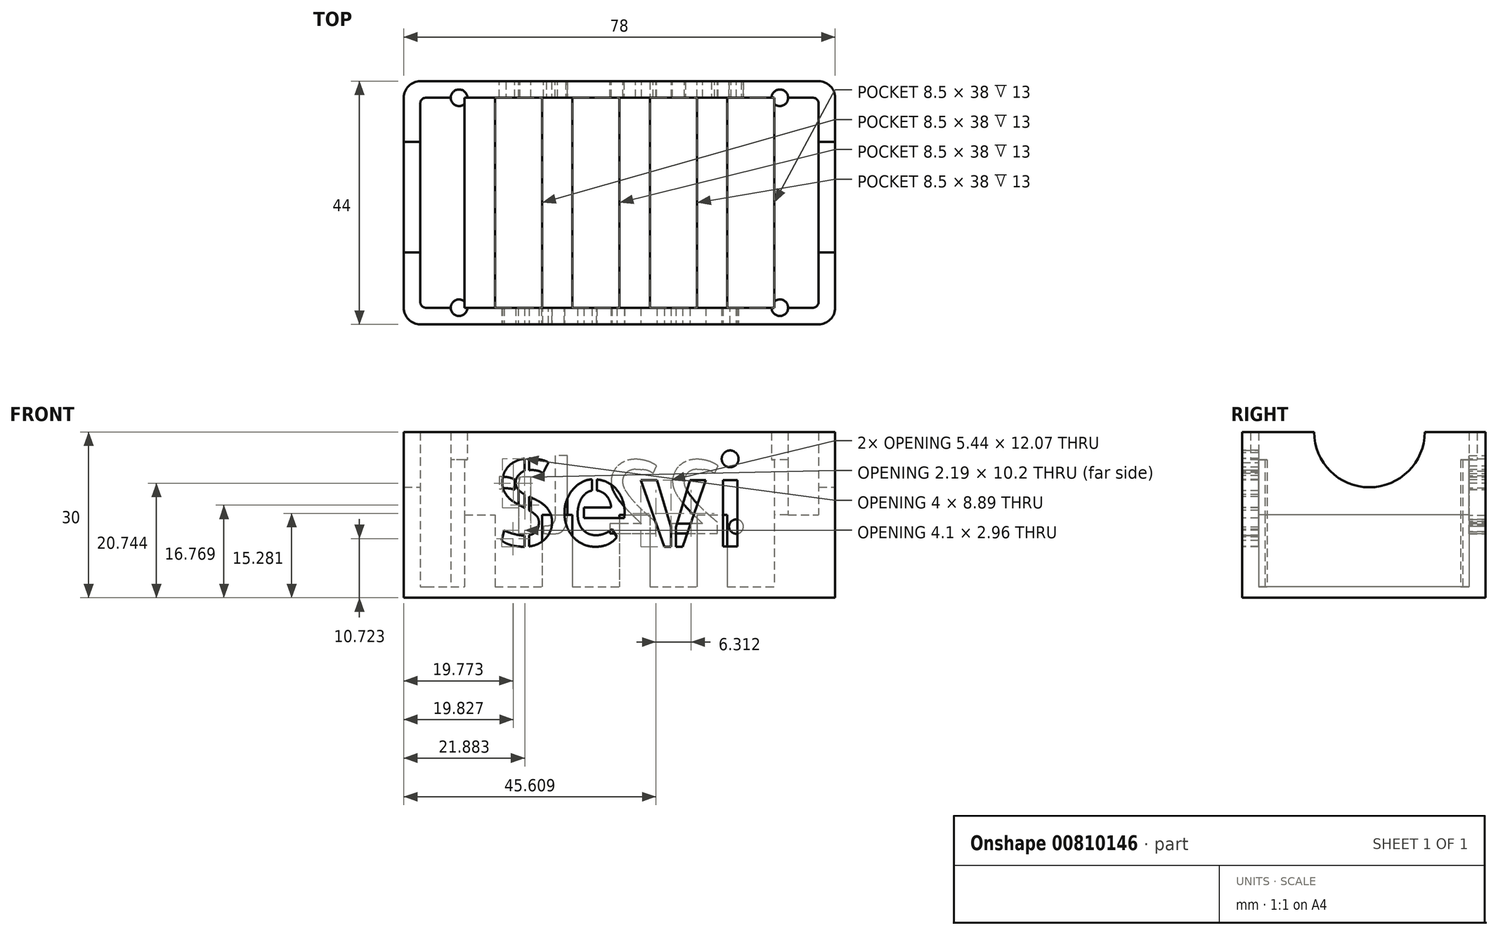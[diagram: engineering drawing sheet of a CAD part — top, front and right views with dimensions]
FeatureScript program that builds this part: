
annotation { "Feature Type Name" : "Feature", "Feature Type Description" : "" }
export const myFeature = defineFeature(function(context is Context, id is Id, definition is map)
    precondition{}
    {
        {
            var Q0;
            Q0=qCreatedBy(makeId("Top.planeOp"),FACE);
            var sketch = newSketch(context, id + "F0", { "sketchPlane" : qUnion([Q0])});
            skLineSegment(sketch, "E0.bottom", {"start": v(-3, 0) * mm, "end": v(-75, 0) * mm});
            skLineSegment(sketch, "E0.top", {"start": v(-3, 44) * mm, "end": v(-75, 44) * mm});
            skLineSegment(sketch, "E0.left", {"start": v(0, 3) * mm, "end": v(0, 41) * mm});
            skLineSegment(sketch, "E0.right", {"start": v(-78, 3) * mm, "end": v(-78, 41) * mm});
            skPoint(sketch, "E1.visualSharp", {"position": v(-78, 44) * mm});
            skArc(sketch, "E1.filletArc", {"start": v(-75, 44) * mm, "mid": v(-77.12, 43.12) * mm, "end": v(-78, 41) * mm});
            skPoint(sketch, "E2.visualSharp", {"position": v(0, 44) * mm});
            skArc(sketch, "E2.filletArc", {"start": v(0, 41) * mm, "mid": v(-0.88, 43.12) * mm, "end": v(-3, 44) * mm});
            skPoint(sketch, "E3.visualSharp", {"position": v(0, 0) * mm});
            skArc(sketch, "E3.filletArc", {"start": v(-3, 0) * mm, "mid": v(-0.88, 0.88) * mm, "end": v(0, 3) * mm});
            skPoint(sketch, "E4.visualSharp", {"position": v(-78, 0) * mm});
            skArc(sketch, "E4.filletArc", {"start": v(-78, 3) * mm, "mid": v(-77.12, 0.88) * mm, "end": v(-75, 0) * mm});
            skSolve(sketch);
        }
        {
            var Q0;
            Q0=makeQuery(id+"F0.imprint","IMPRINT",FACE,{"disambiguationData":[TD([[makeQuery(id+"F0.imprint","IMPRINT",EDGE,{"derivedFrom":sQuery(id+"F0.wireOp",EDGE,"E0.bottom")}),-1.0]])]});
            extrude(context, id + "F1", {"entities" : qUnion([Q0]), "depth" : 30 * mm, "offsetDistance" : 25 * mm});
        }
        {
            var Q0;
            Q0=makeQuery(id+"F1.opExtrude","SWEPT_FACE",FACE,{"disambiguationData":[OSD([sQuery(id+"F0.wireOp",EDGE,"E0.left")])]});
            var sketch = newSketch(context, id + "F2", { "sketchPlane" : qUnion([Q0])});
            skLineSegment(sketch, "E5", {"start": v(41, 2) * mm, "end": v(3, 2) * mm});
            skCircle(sketch, "E6", {"center": v(23, 30) * mm, "radius": 10 * mm});
            skSolve(sketch);
        }
        {
            var Q0;
            Q0=makeQuery(id+"F1.opExtrude","SWEPT_FACE",FACE,{"disambiguationData":[OSD([sQuery(id+"F0.wireOp",EDGE,"E0.top")])]});
            var sketch = newSketch(context, id + "F3", { "sketchPlane" : qUnion([Q0])});
            skLineSegment(sketch, "E7", {"start": v(75, 2) * mm, "end": v(3, 2) * mm});
            skSolve(sketch);
        }
        {
            var Q0;
            Q0=makeQuery(id+"F1.opExtrude","CAP_FACE",FACE,{"disambiguationData":[OSD([sQuery(id+"F0.wireOp",EDGE,"E0.bottom"),sQuery(id+"F0.wireOp",EDGE,"E0.top"),sQuery(id+"F0.wireOp",EDGE,"E0.left"),sQuery(id+"F0.wireOp",EDGE,"E0.right"),sQuery(id+"F0.wireOp",EDGE,"E1.filletArc"),sQuery(id+"F0.wireOp",EDGE,"E2.filletArc"),sQuery(id+"F0.wireOp",EDGE,"E3.filletArc"),sQuery(id+"F0.wireOp",EDGE,"E4.filletArc")])],"isStart":true});
            cPlane(context, id + "F4", {"entities" : qUnion([Q0]), "cplaneType" : CPlaneType.OFFSET, "offset" : 2 * mm, "oppositeDirection" : true, "width" : 150 * mm, "height" : 150 * mm});
        }
        {
            var Q0;
            Q0=qCreatedBy(id+"F4.planeOp",FACE);
            var sketch = newSketch(context, id + "F5", { "sketchPlane" : qUnion([Q0])});
            skLineSegment(sketch, "E8.bottom", {"start": v(-74, -41) * mm, "end": v(-4, -41) * mm});
            skLineSegment(sketch, "E8.top", {"start": v(-74, -3) * mm, "end": v(-4, -3) * mm});
            skLineSegment(sketch, "E8.left", {"start": v(-75, -40) * mm, "end": v(-75, -4) * mm});
            skLineSegment(sketch, "E8.right", {"start": v(-3, -40) * mm, "end": v(-3, -4) * mm});
            skPoint(sketch, "E9.visualSharp", {"position": v(-75, -41) * mm});
            skArc(sketch, "E9.filletArc", {"start": v(-75, -40) * mm, "mid": v(-74.7, -40.7) * mm, "end": v(-74, -41) * mm});
            skPoint(sketch, "E10.visualSharp", {"position": v(-3, -41) * mm});
            skArc(sketch, "E10.filletArc", {"start": v(-4, -41) * mm, "mid": v(-3.3, -40.7) * mm, "end": v(-3, -40) * mm});
            skPoint(sketch, "E11.visualSharp", {"position": v(-75, -3) * mm});
            skArc(sketch, "E11.filletArc", {"start": v(-74, -3) * mm, "mid": v(-74.7, -3.3) * mm, "end": v(-75, -4) * mm});
            skPoint(sketch, "E12.visualSharp", {"position": v(-3, -3) * mm});
            skArc(sketch, "E12.filletArc", {"start": v(-3, -4) * mm, "mid": v(-3.3, -3.3) * mm, "end": v(-4, -3) * mm});
            skLineSegment(sketch, "E13", {"start": v(-67, -41) * mm, "end": v(-67, -3) * mm});
            skLineSegment(sketch, "E14", {"start": v(-67, -3) * mm, "end": v(-61.5, -3) * mm});
            skLineSegment(sketch, "E15", {"start": v(-61.5, -3) * mm, "end": v(-61.5, -41) * mm});
            skLineSegment(sketch, "E16", {"start": v(-61.5, -41) * mm, "end": v(-67, -41) * mm});
            skLineSegment(sketch, "E17", {"start": v(-47.5, -41) * mm, "end": v(-47.5, -3) * mm});
            skLineSegment(sketch, "E18", {"start": v(-53, -3) * mm, "end": v(-47.5, -3) * mm});
            skLineSegment(sketch, "E19", {"start": v(-53, -3) * mm, "end": v(-53, -41) * mm});
            skLineSegment(sketch, "E20", {"start": v(-47.5, -41) * mm, "end": v(-53, -41) * mm});
            skLineSegment(sketch, "E21", {"start": v(-39, -41) * mm, "end": v(-39, -3) * mm});
            skLineSegment(sketch, "E22", {"start": v(-39, -3) * mm, "end": v(-33.5, -3) * mm});
            skLineSegment(sketch, "E23", {"start": v(-33.5, -3) * mm, "end": v(-33.5, -41) * mm});
            skLineSegment(sketch, "E24", {"start": v(-33.5, -41) * mm, "end": v(-39, -41) * mm});
            skLineSegment(sketch, "E25", {"start": v(-25, -41) * mm, "end": v(-25, -3) * mm});
            skLineSegment(sketch, "E26", {"start": v(-25, -3) * mm, "end": v(-19.5, -3) * mm});
            skLineSegment(sketch, "E27", {"start": v(-19.5, -3) * mm, "end": v(-19.5, -41) * mm});
            skLineSegment(sketch, "E28", {"start": v(-19.5, -41) * mm, "end": v(-25, -41) * mm});
            skLineSegment(sketch, "E29", {"start": v(-11, -41) * mm, "end": v(-11, -3) * mm});
            skLineSegment(sketch, "E30", {"start": v(-11, -3) * mm, "end": v(-5, -3) * mm});
            skLineSegment(sketch, "E31", {"start": v(-5, -3) * mm, "end": v(-5, -41) * mm});
            skLineSegment(sketch, "E32", {"start": v(-5, -41) * mm, "end": v(-11, -41) * mm});
            skLineSegment(sketch, "E33", {"start": v(-53, -41) * mm, "end": v(-47.5, -41) * mm});
            skLineSegment(sketch, "E34", {"start": v(-39, -41) * mm, "end": v(-33.5, -41) * mm});
            skLineSegment(sketch, "E35", {"start": v(-33.5, -3) * mm, "end": v(-39, -3) * mm});
            skLineSegment(sketch, "E36", {"start": v(-11, -41) * mm, "end": v(-3, -41) * mm});
            skLineSegment(sketch, "E37", {"start": v(-3, -3) * mm, "end": v(-11, -3) * mm});
            skCircle(sketch, "E38", {"center": v(-68, -41) * mm, "radius": 1.5 * mm});
            skCircle(sketch, "E39", {"center": v(-68, -3) * mm, "radius": 1.5 * mm});
            skCircle(sketch, "E40", {"center": v(-10, -41) * mm, "radius": 1.5 * mm});
            skCircle(sketch, "E41", {"center": v(-10, -3) * mm, "radius": 1.5 * mm});
            skSolve(sketch);
        }
        {
            var Q0;
            {var subQ2=sQuery(id+"F5.wireOp",EDGE,"E8.top");var subQ3=sQuery(id+"F5.wireOp",EDGE,"E31");var subQ5=makeQuery(id+"F5.imprint","IMPRINT",EDGE,{"derivedFrom":subQ3});var subQ6=sQuery(id+"F5.wireOp",EDGE,"E8.bottom");var subQ8=sQuery(id+"F5.wireOp",EDGE,"E25");var subQ10=sQuery(id+"F5.wireOp",EDGE,"E27");var subQ14=makeQuery(id+"F5.imprint","IMPRINT",EDGE,{"derivedFrom":subQ8});var subQ15=makeQuery(id+"F5.imprint","IMPRINT",EDGE,{"derivedFrom":subQ10});var subQ16=sQuery(id+"F5.wireOp",EDGE,"E39");var subQ17=makeQuery(id+"F5.imprint","INTERSECT",VERTEX,{"disambiguationData":[OD(1.0)],"derivedFrom":[subQ2,subQ16]});var subQ20=makeQuery(id+"F5.imprint","IMPRINT",EDGE,{"disambiguationData":[TD([[subQ17,-1.0]])],"derivedFrom":subQ2});var subQ24=makeQuery(id+"F5.imprint","INTERSECT",VERTEX,{"disambiguationData":[OD(0.0)],"derivedFrom":[subQ2,subQ16]});var subQ25=makeQuery(id+"F5.imprint","IMPRINT",EDGE,{"disambiguationData":[TD([[subQ24,1.0]])],"derivedFrom":subQ2});var subQ27=sQuery(id+"F5.wireOp",EDGE,"E38");var subQ28=makeQuery(id+"F5.imprint","INTERSECT",VERTEX,{"disambiguationData":[OD(1.0)],"derivedFrom":[subQ6,subQ27]});var subQ30=makeQuery(id+"F5.imprint","IMPRINT",EDGE,{"disambiguationData":[TD([[subQ28,-1.0]])],"derivedFrom":subQ6});var subQ34=sQuery(id+"F5.wireOp",EDGE,"E29");var subQ35=makeQuery(id+"F5.imprint","INTERSECT",VERTEX,{"derivedFrom":[subQ2,subQ34]});var subQ38=makeQuery(id+"F5.imprint","IMPRINT",EDGE,{"disambiguationData":[TD([[subQ35,1.0]])],"derivedFrom":subQ2});var subQ42=sQuery(id+"F5.wireOp",EDGE,"E21");var subQ44=sQuery(id+"F5.wireOp",EDGE,"E23");var subQ48=makeQuery(id+"F5.imprint","IMPRINT",EDGE,{"derivedFrom":subQ42});var subQ49=makeQuery(id+"F5.imprint","IMPRINT",EDGE,{"derivedFrom":subQ44});var subQ53=sQuery(id+"F5.wireOp",EDGE,"E40");var subQ56=makeQuery(id+"F5.imprint","INTERSECT",VERTEX,{"disambiguationData":[OD(0.0)],"derivedFrom":[subQ6,subQ53]});var subQ59=makeQuery(id+"F5.imprint","IMPRINT",EDGE,{"disambiguationData":[TD([[subQ56,-1.0]])],"derivedFrom":subQ6});var subQ61=sQuery(id+"F5.wireOp",EDGE,"E17");var subQ67=makeQuery(id+"F5.imprint","IMPRINT",EDGE,{"derivedFrom":subQ61});var subQ69=sQuery(id+"F5.wireOp",EDGE,"E15");var subQ70=makeQuery(id+"F5.imprint","IMPRINT",EDGE,{"derivedFrom":subQ69});var subQ72=makeQuery(id+"F5.imprint","INTERSECT",VERTEX,{"disambiguationData":[OD(0.0)],"derivedFrom":[subQ6,subQ27]});var subQ75=makeQuery(id+"F5.imprint","INTERSECT",VERTEX,{"disambiguationData":[OD(1.0)],"derivedFrom":[subQ6,subQ53]});var subQ76=makeQuery(id+"F5.imprint","IMPRINT",EDGE,{"disambiguationData":[TD([[subQ75,1.0]])],"derivedFrom":subQ6});var subQ79=makeQuery(id+"F5.imprint","IMPRINT",EDGE,{"disambiguationData":[TD([[subQ35,-1.0]])],"derivedFrom":subQ2});var subQ80=makeQuery(id+"F5.imprint","IMPRINT",EDGE,{"disambiguationData":[TD([[subQ72,1.0]])],"derivedFrom":subQ6});Q0=qUnion([makeQuery(id+"F5.imprint","IMPRINT",FACE,{"disambiguationData":[TD([[subQ79,-1.0]])]}),makeQuery(id+"F5.imprint","IMPRINT",FACE,{"disambiguationData":[TD([[subQ30,-1.0]])]}),makeQuery(id+"F5.imprint","IMPRINT",FACE,{"disambiguationData":[TD([[subQ67,-1.0]])]}),makeQuery(id+"F5.imprint","IMPRINT",FACE,{"disambiguationData":[TD([[subQ76,-1.0]])]}),makeQuery(id+"F5.imprint","IMPRINT",FACE,{"disambiguationData":[TD([[subQ5,-1.0]])]}),makeQuery(id+"F5.imprint","IMPRINT",FACE,{"disambiguationData":[TD([[subQ49,1.0]])]}),makeQuery(id+"F5.imprint","IMPRINT",FACE,{"disambiguationData":[TD([[subQ80,1.0]])]}),makeQuery(id+"F5.imprint","IMPRINT",FACE,{"disambiguationData":[TD([[subQ79,1.0]])]}),makeQuery(id+"F5.imprint","IMPRINT",FACE,{"disambiguationData":[TD([[subQ70,1.0]])]}),makeQuery(id+"F5.imprint","IMPRINT",FACE,{"disambiguationData":[TD([[subQ76,1.0]])]}),makeQuery(id+"F5.imprint","IMPRINT",FACE,{"disambiguationData":[TD([[subQ70,-1.0]])]}),makeQuery(id+"F5.imprint","IMPRINT",FACE,{"disambiguationData":[TD([[subQ20,1.0]])]}),makeQuery(id+"F5.imprint","IMPRINT",FACE,{"disambiguationData":[TD([[subQ67,1.0]])]}),makeQuery(id+"F5.imprint","IMPRINT",FACE,{"disambiguationData":[TD([[subQ59,1.0]])]}),makeQuery(id+"F5.imprint","IMPRINT",FACE,{"disambiguationData":[TD([[subQ15,1.0]])]}),makeQuery(id+"F5.imprint","IMPRINT",FACE,{"disambiguationData":[TD([[makeQuery(id+"F5.imprint","IMPRINT",EDGE,{"derivedFrom":sQuery(id+"F5.wireOp",EDGE,"E8.left")}),-1.0]])]}),makeQuery(id+"F5.imprint","IMPRINT",FACE,{"disambiguationData":[TD([[subQ48,-1.0]])]}),makeQuery(id+"F5.imprint","IMPRINT",FACE,{"disambiguationData":[TD([[subQ38,-1.0]])]}),makeQuery(id+"F5.imprint","IMPRINT",FACE,{"disambiguationData":[TD([[subQ30,1.0]])]}),makeQuery(id+"F5.imprint","IMPRINT",FACE,{"disambiguationData":[TD([[subQ25,-1.0]])]}),makeQuery(id+"F5.imprint","IMPRINT",FACE,{"disambiguationData":[TD([[subQ20,-1.0]])]}),makeQuery(id+"F5.imprint","IMPRINT",FACE,{"disambiguationData":[TD([[subQ14,-1.0]])]}),makeQuery(id+"F5.imprint","IMPRINT",FACE,{"disambiguationData":[TD([[makeQuery(id+"F5.imprint","IMPRINT",EDGE,{"derivedFrom":sQuery(id+"F5.wireOp",EDGE,"E8.right")}),1.0]])]})]);}
            extrude(context, id + "F6", {"entities" : qUnion([Q0]), "operationType" : NewBodyOperationType.REMOVE, "oppositeDirection" : true, "depth" : 38 * mm, "offsetDistance" : 25 * mm});
        }
        {
            var Q0;
            {var subQ0=sQuery(id+"F5.wireOp",EDGE,"E39");var subQ1=sQuery(id+"F5.wireOp",EDGE,"E8.top");var subQ2=makeQuery(id+"F5.imprint","INTERSECT",VERTEX,{"disambiguationData":[OD(0.0)],"derivedFrom":[subQ1,subQ0]});var subQ6=sQuery(id+"F5.wireOp",EDGE,"E38");var subQ7=sQuery(id+"F5.wireOp",EDGE,"E8.bottom");var subQ8=makeQuery(id+"F5.imprint","INTERSECT",VERTEX,{"disambiguationData":[OD(0.0)],"derivedFrom":[subQ7,subQ6]});Q0=qUnion([makeQuery(id+"F5.imprint","IMPRINT",FACE,{"disambiguationData":[TD([[makeQuery(id+"F5.imprint","IMPRINT",EDGE,{"disambiguationData":[TD([[subQ8,1.0]])],"derivedFrom":subQ7}),1.0]])]}),makeQuery(id+"F5.imprint","IMPRINT",FACE,{"disambiguationData":[TD([[makeQuery(id+"F5.imprint","IMPRINT",EDGE,{"disambiguationData":[TD([[subQ2,1.0]])],"derivedFrom":subQ1}),-1.0]])]})]);}
            var Q1;
            {var subQ0=sQuery(id+"F5.wireOp",EDGE,"E17");Q1=makeQuery(id+"F5.imprint","IMPRINT",FACE,{"disambiguationData":[TD([[makeQuery(id+"F5.imprint","IMPRINT",EDGE,{"derivedFrom":subQ0}),1.0]])]});}
            var Q2;
            {var subQ0=sQuery(id+"F5.wireOp",EDGE,"E21");Q2=makeQuery(id+"F5.imprint","IMPRINT",FACE,{"disambiguationData":[TD([[makeQuery(id+"F5.imprint","IMPRINT",EDGE,{"derivedFrom":subQ0}),-1.0]])]});}
            var Q3;
            {var subQ0=sQuery(id+"F5.wireOp",EDGE,"E25");Q3=makeQuery(id+"F5.imprint","IMPRINT",FACE,{"disambiguationData":[TD([[makeQuery(id+"F5.imprint","IMPRINT",EDGE,{"derivedFrom":subQ0}),-1.0]])]});}
            var Q4;
            Q4=makeQuery(id+"F5.imprint","IMPRINT",FACE,{"disambiguationData":[TD([[makeQuery(id+"F5.imprint","IMPRINT",EDGE,{"derivedFrom":sQuery(id+"F5.wireOp",EDGE,"E8.right")}),1.0]])]});
            var Q5;
            {var subQ0=sQuery(id+"F5.wireOp",EDGE,"E15");Q5=makeQuery(id+"F5.imprint","IMPRINT",FACE,{"disambiguationData":[TD([[makeQuery(id+"F5.imprint","IMPRINT",EDGE,{"derivedFrom":subQ0}),-1.0]])]});}
            var Q6;
            {var subQ5=sQuery(id+"F5.wireOp",EDGE,"E31");Q6=makeQuery(id+"F5.imprint","IMPRINT",FACE,{"disambiguationData":[TD([[makeQuery(id+"F5.imprint","IMPRINT",EDGE,{"derivedFrom":subQ5}),-1.0]])]});}
            extrude(context, id + "F7", {"entities" : qUnion([Q0, Q1, Q2, Q3, Q4, Q5, Q6]), "operationType" : NewBodyOperationType.ADD, "oppositeDirection" : true, "depth" : 13 * mm, "offsetDistance" : 25 * mm});
        }
        {
            var Q0;
            {var subQ0=sQuery(id+"F2.wireOp",EDGE,"E6");var subQ1=makeQuery(id+"F1.opExtrude","CAP_EDGE",EDGE,{"disambiguationData":[OSD([sQuery(id+"F0.wireOp",EDGE,"E0.left")])],"isStart":false});var subQ2=makeQuery(id+"F2.imprint","INTERSECT",VERTEX,{"disambiguationData":[OD(0.0)],"derivedFrom":[subQ1,subQ0]});Q0=makeQuery(id+"F2.imprint","IMPRINT",FACE,{"disambiguationData":[TD([[makeQuery(id+"F2.imprint","IMPRINT",EDGE,{"disambiguationData":[TD([[subQ2,-1.0]])],"derivedFrom":subQ0}),1.0]])]});}
            extrude(context, id + "F8", {"entities" : qUnion([Q0]), "operationType" : NewBodyOperationType.REMOVE, "oppositeDirection" : true, "depth" : 80 * mm, "offsetDistance" : 25 * mm});
        }
        {
            var Q0;
            {var subQ0=sQuery(id+"F5.wireOp",EDGE,"E38");var subQ1=sQuery(id+"F5.wireOp",EDGE,"E8.bottom");var subQ2=makeQuery(id+"F5.imprint","INTERSECT",VERTEX,{"disambiguationData":[OD(1.0)],"derivedFrom":[subQ1,subQ0]});Q0=makeQuery(id+"F5.imprint","IMPRINT",FACE,{"disambiguationData":[TD([[makeQuery(id+"F5.imprint","IMPRINT",EDGE,{"disambiguationData":[TD([[subQ2,-1.0]])],"derivedFrom":subQ1}),1.0]])]});}
            var Q1;
            {var subQ0=sQuery(id+"F5.wireOp",EDGE,"E38");var subQ1=sQuery(id+"F5.wireOp",EDGE,"E8.bottom");var subQ2=makeQuery(id+"F5.imprint","INTERSECT",VERTEX,{"disambiguationData":[OD(1.0)],"derivedFrom":[subQ1,subQ0]});Q1=makeQuery(id+"F5.imprint","IMPRINT",FACE,{"disambiguationData":[TD([[makeQuery(id+"F5.imprint","IMPRINT",EDGE,{"disambiguationData":[TD([[subQ2,-1.0]])],"derivedFrom":subQ1}),-1.0]])]});}
            var Q2;
            {var subQ0=sQuery(id+"F5.wireOp",EDGE,"E40");var subQ1=sQuery(id+"F5.wireOp",EDGE,"E8.bottom");var subQ2=makeQuery(id+"F5.imprint","INTERSECT",VERTEX,{"disambiguationData":[OD(1.0)],"derivedFrom":[subQ1,subQ0]});Q2=makeQuery(id+"F5.imprint","IMPRINT",FACE,{"disambiguationData":[TD([[makeQuery(id+"F5.imprint","IMPRINT",EDGE,{"disambiguationData":[TD([[subQ2,1.0]])],"derivedFrom":subQ1}),-1.0]])]});}
            var Q3;
            {var subQ0=sQuery(id+"F5.wireOp",EDGE,"E40");var subQ1=sQuery(id+"F5.wireOp",EDGE,"E8.bottom");var subQ2=makeQuery(id+"F5.imprint","INTERSECT",VERTEX,{"disambiguationData":[OD(1.0)],"derivedFrom":[subQ1,subQ0]});Q3=makeQuery(id+"F5.imprint","IMPRINT",FACE,{"disambiguationData":[TD([[makeQuery(id+"F5.imprint","IMPRINT",EDGE,{"disambiguationData":[TD([[subQ2,1.0]])],"derivedFrom":subQ1}),1.0]])]});}
            var Q4;
            {var subQ0=sQuery(id+"F5.wireOp",EDGE,"E29");var subQ1=sQuery(id+"F5.wireOp",EDGE,"E8.top");var subQ2=makeQuery(id+"F5.imprint","INTERSECT",VERTEX,{"derivedFrom":[subQ1,subQ0]});Q4=makeQuery(id+"F5.imprint","IMPRINT",FACE,{"disambiguationData":[TD([[makeQuery(id+"F5.imprint","IMPRINT",EDGE,{"disambiguationData":[TD([[subQ2,-1.0]])],"derivedFrom":subQ1}),-1.0]])]});}
            var Q5;
            {var subQ0=sQuery(id+"F5.wireOp",EDGE,"E8.top");var subQ1=makeQuery(id+"F5.imprint","INTERSECT",VERTEX,{"derivedFrom":[subQ0,sQuery(id+"F5.wireOp",EDGE,"E29")]});Q5=makeQuery(id+"F5.imprint","IMPRINT",FACE,{"disambiguationData":[TD([[makeQuery(id+"F5.imprint","IMPRINT",EDGE,{"disambiguationData":[TD([[subQ1,-1.0]])],"derivedFrom":subQ0}),1.0]])]});}
            var Q6;
            {var subQ0=sQuery(id+"F5.wireOp",EDGE,"E39");var subQ1=sQuery(id+"F5.wireOp",EDGE,"E8.top");var subQ2=makeQuery(id+"F5.imprint","INTERSECT",VERTEX,{"disambiguationData":[OD(1.0)],"derivedFrom":[subQ1,subQ0]});Q6=makeQuery(id+"F5.imprint","IMPRINT",FACE,{"disambiguationData":[TD([[makeQuery(id+"F5.imprint","IMPRINT",EDGE,{"disambiguationData":[TD([[subQ2,-1.0]])],"derivedFrom":subQ1}),-1.0]])]});}
            var Q7;
            {var subQ0=sQuery(id+"F5.wireOp",EDGE,"E39");var subQ1=sQuery(id+"F5.wireOp",EDGE,"E8.top");var subQ2=makeQuery(id+"F5.imprint","INTERSECT",VERTEX,{"disambiguationData":[OD(1.0)],"derivedFrom":[subQ1,subQ0]});Q7=makeQuery(id+"F5.imprint","IMPRINT",FACE,{"disambiguationData":[TD([[makeQuery(id+"F5.imprint","IMPRINT",EDGE,{"disambiguationData":[TD([[subQ2,-1.0]])],"derivedFrom":subQ1}),1.0]])]});}
            extrude(context, id + "F9", {"entities" : qUnion([Q0, Q1, Q2, Q3, Q4, Q5, Q6, Q7]), "operationType" : NewBodyOperationType.ADD, "oppositeDirection" : true, "depth" : 23 * mm, "offsetDistance" : 25 * mm});
        }
        {
            var Q0;
            {var subQ0=sQuery(id+"F5.wireOp",EDGE,"E40");var subQ1=sQuery(id+"F5.wireOp",EDGE,"E8.bottom");var subQ2=makeQuery(id+"F5.imprint","INTERSECT",VERTEX,{"disambiguationData":[OD(1.0)],"derivedFrom":[subQ1,subQ0]});var subQ3=sQuery(id+"F5.wireOp",EDGE,"E29");var subQ6=sQuery(id+"F5.wireOp",EDGE,"E8.top");var subQ7=makeQuery(id+"F5.imprint","INTERSECT",VERTEX,{"derivedFrom":[subQ6,subQ3]});Q0=qUnion([makeQuery(id+"F5.imprint","IMPRINT",FACE,{"disambiguationData":[TD([[makeQuery(id+"F5.imprint","IMPRINT",EDGE,{"disambiguationData":[TD([[subQ7,-1.0]])],"derivedFrom":subQ6}),-1.0]])]}),makeQuery(id+"F5.imprint","IMPRINT",FACE,{"disambiguationData":[TD([[makeQuery(id+"F5.imprint","IMPRINT",EDGE,{"disambiguationData":[TD([[subQ2,1.0]])],"derivedFrom":subQ1}),1.0]])]})]);}
            extrude(context, id + "F10", {"entities" : qUnion([Q0]), "operationType" : NewBodyOperationType.ADD, "oppositeDirection" : true, "depth" : 13 * mm, "offsetDistance" : 25 * mm});
        }
        {
            var Q0;
            Q0=makeQuery(id+"F1.opExtrude","SWEPT_FACE",FACE,{"disambiguationData":[OSD([sQuery(id+"F0.wireOp",EDGE,"E0.bottom")])]});
            var sketch = newSketch(context, id + "F11", { "sketchPlane" : qUnion([Q0])});
            skText(sketch, "E42", { "text": "Sevi", "fontName": "AllertaStencil-Regular.ttf"});
            const initialGuessF11  = {"E42": [-0.062, 0.00933, 1, 0, 0.01567]};
            skSetInitialGuess(sketch, initialGuessF11);
            skSolve(sketch);
        }
        {
            var Q0;
            Q0 = qSketchRegion(id + "F11", true);
            extrude(context, id + "F12", {"entities" : qUnion([Q0]), "operationType" : NewBodyOperationType.REMOVE, "oppositeDirection" : true, "depth" : 3 * mm, "offsetDistance" : 25 * mm});
        }
        {
            var Q0;
            Q0=makeQuery(id+"F1.opExtrude","SWEPT_FACE",FACE,{"disambiguationData":[OSD([sQuery(id+"F0.wireOp",EDGE,"E0.top")])]});
            var sketch = newSketch(context, id + "F13", { "sketchPlane" : qUnion([Q0])});
            skText(sketch, "E43", { "text": ".22 lr", "fontName": "AllertaStencil-Regular.ttf"});
            const initialGuessF13  = {"E43": [0.016, 0.01167, 1, 0, 0.01333]};
            skSetInitialGuess(sketch, initialGuessF13);
            skSolve(sketch);
        }
        {
            var Q0;
            Q0 = qSketchRegion(id + "F13", true);
            extrude(context, id + "F14", {"entities" : qUnion([Q0]), "operationType" : NewBodyOperationType.REMOVE, "oppositeDirection" : true, "depth" : 3 * mm, "offsetDistance" : 25 * mm});
        }
    });
